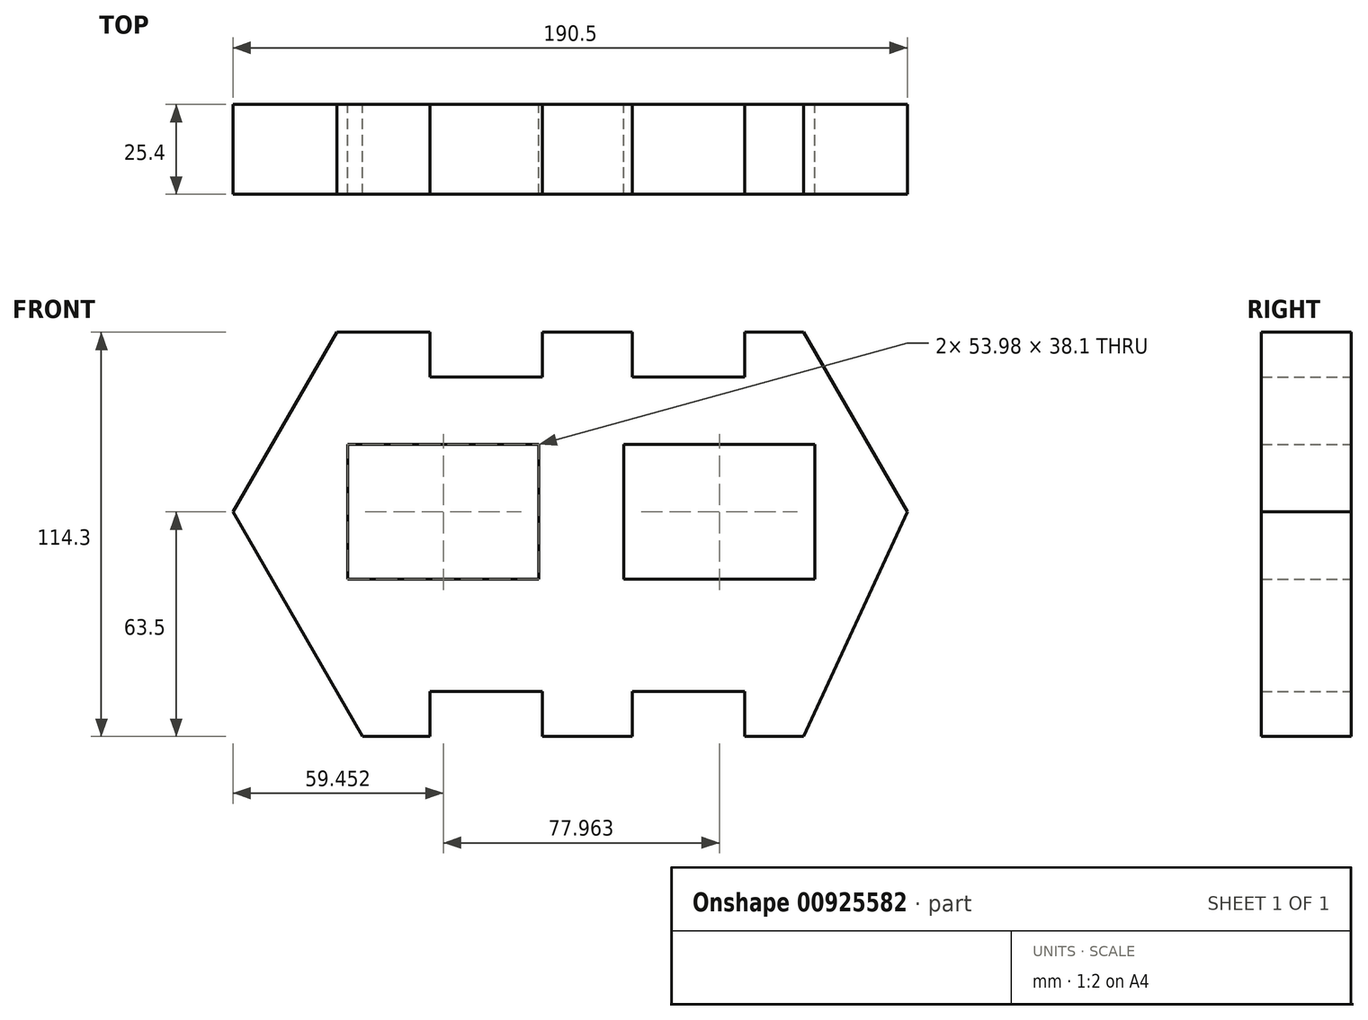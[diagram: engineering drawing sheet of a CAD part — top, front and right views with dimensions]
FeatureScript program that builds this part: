
annotation { "Feature Type Name" : "Feature", "Feature Type Description" : "" }
export const myFeature = defineFeature(function(context is Context, id is Id, definition is map)
    precondition{}
    {
        {
            var Q0;
            Q0=qCreatedBy(makeId("Front.planeOp"),FACE);
            var sketch = newSketch(context, id + "F0", { "sketchPlane" : qUnion([Q0])});
            skLineSegment(sketch, "E0", {"start": v(-68.56, 50.8) * mm, "end": v(-97.9, 0) * mm});
            skLineSegment(sketch, "E1", {"start": v(-97.9, 0) * mm, "end": v(-61.23, -63.5) * mm});
            skLineSegment(sketch, "E2", {"start": v(-68.56, 50.8) * mm, "end": v(-42.21, 50.8) * mm});
            skLineSegment(sketch, "E3", {"start": v(-42.21, 50.8) * mm, "end": v(-42.21, 38.1) * mm});
            skLineSegment(sketch, "E4", {"start": v(-42.21, 38.1) * mm, "end": v(-10.46, 38.1) * mm});
            skLineSegment(sketch, "E5", {"start": v(-10.46, 38.1) * mm, "end": v(-10.46, 50.8) * mm});
            skLineSegment(sketch, "E6", {"start": v(-10.46, 50.8) * mm, "end": v(14.94, 50.8) * mm});
            skLineSegment(sketch, "E7", {"start": v(14.94, 50.8) * mm, "end": v(14.94, 38.1) * mm});
            skLineSegment(sketch, "E8", {"start": v(46.69, 38.1) * mm, "end": v(14.94, 38.1) * mm});
            skLineSegment(sketch, "E9", {"start": v(46.69, 38.1) * mm, "end": v(46.69, 50.8) * mm});
            skLineSegment(sketch, "E10", {"start": v(46.69, 50.8) * mm, "end": v(63.28, 50.8) * mm});
            skLineSegment(sketch, "E11", {"start": v(63.28, 50.8) * mm, "end": v(92.6, 0) * mm});
            skLineSegment(sketch, "E12", {"start": v(63.28, -63.5) * mm, "end": v(92.6, 0) * mm});
            skLineSegment(sketch, "E13", {"start": v(46.69, -63.5) * mm, "end": v(63.28, -63.5) * mm});
            skLineSegment(sketch, "E14", {"start": v(46.69, -50.8) * mm, "end": v(46.69, -63.5) * mm});
            skLineSegment(sketch, "E15", {"start": v(46.69, -50.8) * mm, "end": v(14.94, -50.8) * mm});
            skLineSegment(sketch, "E16", {"start": v(14.94, -63.5) * mm, "end": v(14.94, -50.8) * mm});
            skLineSegment(sketch, "E17", {"start": v(-10.46, -63.5) * mm, "end": v(14.94, -63.5) * mm});
            skLineSegment(sketch, "E18", {"start": v(-10.46, -50.8) * mm, "end": v(-10.46, -63.5) * mm});
            skLineSegment(sketch, "E19", {"start": v(-42.21, -50.8) * mm, "end": v(-10.46, -50.8) * mm});
            skLineSegment(sketch, "E20", {"start": v(-42.21, -63.5) * mm, "end": v(-42.21, -50.8) * mm});
            skLineSegment(sketch, "E21", {"start": v(-61.23, -63.5) * mm, "end": v(-42.21, -63.5) * mm});
            skLineSegment(sketch, "E22.bottom", {"start": v(-65.43, 19.05) * mm, "end": v(-11.45, 19.05) * mm});
            skLineSegment(sketch, "E22.top", {"start": v(-65.43, -19.05) * mm, "end": v(-11.45, -19.05) * mm});
            skLineSegment(sketch, "E22.left", {"start": v(-65.43, 19.05) * mm, "end": v(-65.43, -19.05) * mm});
            skLineSegment(sketch, "E22.right", {"start": v(-11.45, 19.05) * mm, "end": v(-11.45, -19.05) * mm});
            skLineSegment(sketch, "E23.bottom", {"start": v(12.54, 19.05) * mm, "end": v(66.51, 19.05) * mm});
            skLineSegment(sketch, "E23.top", {"start": v(12.54, -19.05) * mm, "end": v(66.51, -19.05) * mm});
            skLineSegment(sketch, "E23.left", {"start": v(12.54, 19.05) * mm, "end": v(12.54, -19.05) * mm});
            skLineSegment(sketch, "E23.right", {"start": v(66.51, 19.05) * mm, "end": v(66.51, -19.05) * mm});
            skSolve(sketch);
        }
        {
            var Q0;
            Q0=makeQuery(id+"F0.imprint","IMPRINT",FACE,{"disambiguationData":[TD([[makeQuery(id+"F0.imprint","IMPRINT",EDGE,{"derivedFrom":sQuery(id+"F0.wireOp",EDGE,"E0")}),1.0]])]});
            extrude(context, id + "F1", {"entities" : qUnion([Q0]), "depth" : 25.4 * mm, "offsetDistance" : 25.4 * mm});
        }
    });
